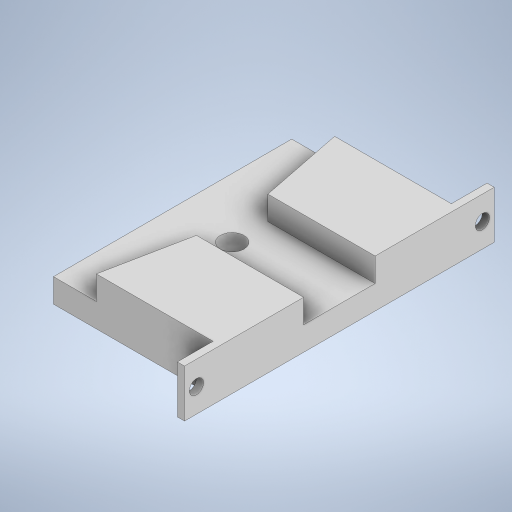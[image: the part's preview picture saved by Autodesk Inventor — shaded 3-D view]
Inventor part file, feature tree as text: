
AUTODESK INVENTOR PART (.ipt)
format: ipt  version: 2023 (Build 270158000, 158)  size: 292,864 bytes
history: native  units: mm
features: extrude x5, sketch x4, other x1, chamfer x1
ambient origin geometry x8: Origin, YZ Plane, XZ Plane, XY Plane, X Axis, Y Axis, Z Axis, Center Point
bodies: Body1 (feature_tree)
feature tree (11):
  other  "Твердое тело1"
  extrude  "Выдавливание1"  Depth=70.0mm
  sketch  "Эскиз2"
  extrude  "Выдавливание2"  Depth=100.0mm
  extrude  "Выдавливание3"  Depth=10.0mm TaperAngle=0.0deg
  extrude  "Выдавливание4"  Depth=45.0mm
  chamfer  "Фаска1"  Distance=10.0mm
  extrude  "Выдавливание5"  Depth=15.0mm
  sketch  "Эскиз1"
  sketch  "Эскиз3"
  sketch  "Эскиз4"
